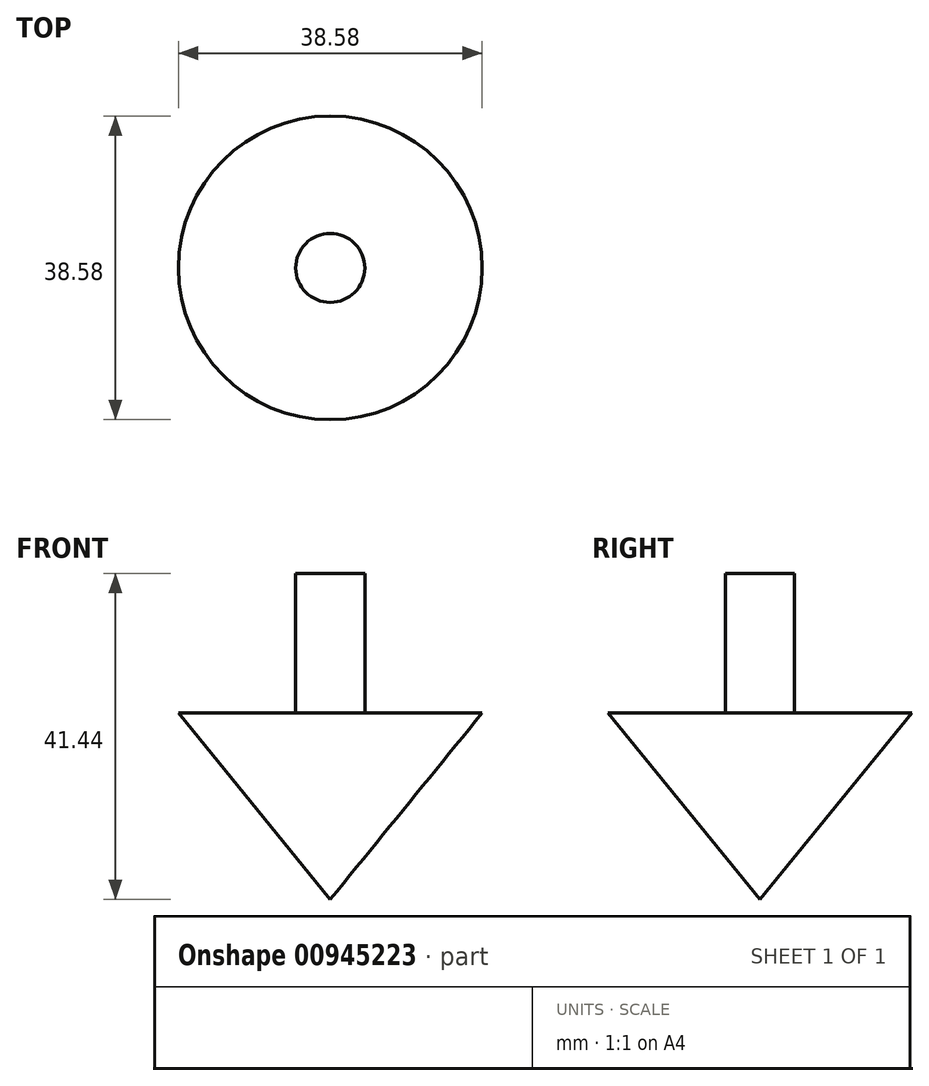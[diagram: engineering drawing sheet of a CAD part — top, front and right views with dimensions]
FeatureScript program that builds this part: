
annotation { "Feature Type Name" : "Feature", "Feature Type Description" : "" }
export const myFeature = defineFeature(function(context is Context, id is Id, definition is map)
    precondition{}
    {
        {
            var Q0;
            Q0=qCreatedBy(makeId("Right.planeOp"),FACE);
            var sketch = newSketch(context, id + "F0", { "sketchPlane" : qUnion([Q0])});
            skLineSegment(sketch, "E0", {"start": v(0, 26.23) * mm, "end": v(4.39, 26.23) * mm});
            skLineSegment(sketch, "E1", {"start": v(4.39, 26.23) * mm, "end": v(4.39, 8.47) * mm});
            skLineSegment(sketch, "E2", {"start": v(4.39, 8.47) * mm, "end": v(19.29, 8.47) * mm});
            skLineSegment(sketch, "E3", {"start": v(19.29, 8.47) * mm, "end": v(0, -15.2) * mm});
            skLineSegment(sketch, "E4", {"start": v(0, -15.2) * mm, "end": v(0, 26.23) * mm});
            skSolve(sketch);
        }
        {
            var Q0;
            Q0=makeQuery(id+"F0.imprint","IMPRINT",FACE,{"disambiguationData":[TD([[makeQuery(id+"F0.imprint","IMPRINT",EDGE,{"derivedFrom":sQuery(id+"F0.wireOp",EDGE,"E0")}),-1.0]])]});
            var Q1;
            Q1=sQuery(id+"F0.wireOp",EDGE,"E4");
            revolve(context, id + "F1", {"surfaceOperationType" : NewSurfaceOperationType.NEW, "entities" : qUnion([Q0]), "axis" : qUnion([Q1]), "revolveType" : RevolveType.FULL});
        }
    });
